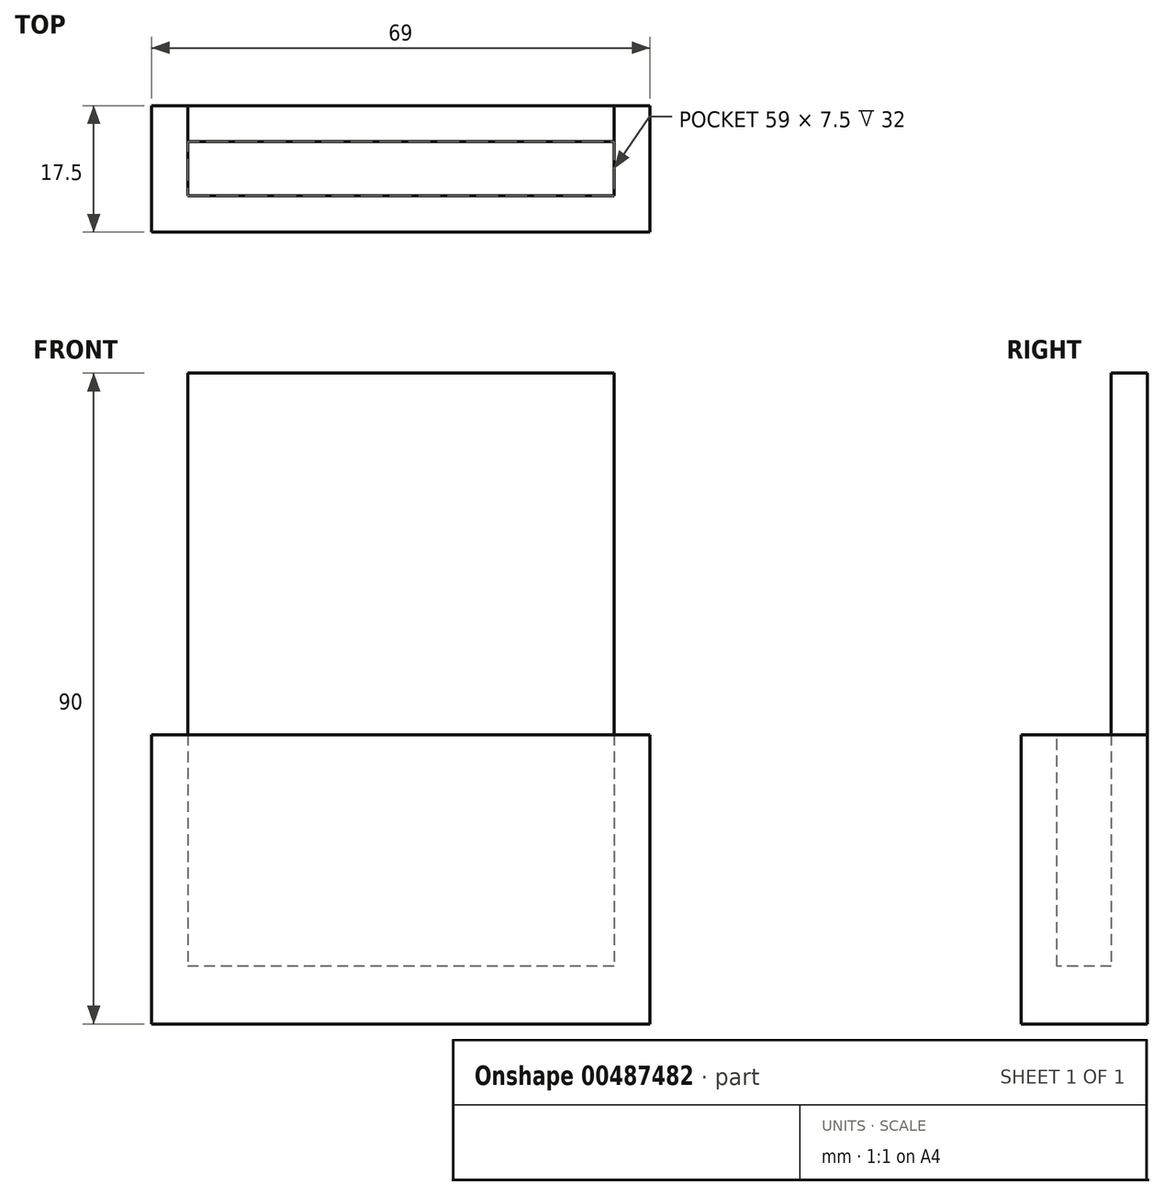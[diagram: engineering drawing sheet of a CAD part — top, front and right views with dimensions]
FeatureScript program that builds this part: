
annotation { "Feature Type Name" : "Feature", "Feature Type Description" : "" }
export const myFeature = defineFeature(function(context is Context, id is Id, definition is map)
    precondition{}
    {
        {
            var Q0;
            Q0=qCreatedBy(makeId("Right.planeOp"),FACE);
            var sketch = newSketch(context, id + "F0", { "sketchPlane" : qUnion([Q0])});
            skLineSegment(sketch, "E0", {"start": v(0, 0) * mm, "end": v(0, 90) * mm});
            skLineSegment(sketch, "E1", {"start": v(0, 90) * mm, "end": v(-5, 90) * mm});
            skLineSegment(sketch, "E2", {"start": v(-5, 90) * mm, "end": v(-5, 8) * mm});
            skLineSegment(sketch, "E3", {"start": v(-5, 8) * mm, "end": v(-12.5, 8) * mm});
            skLineSegment(sketch, "E4", {"start": v(-12.5, 8) * mm, "end": v(-12.5, 40) * mm});
            skLineSegment(sketch, "E5", {"start": v(-12.5, 40) * mm, "end": v(-17.5, 40) * mm});
            skLineSegment(sketch, "E6", {"start": v(-17.5, 40) * mm, "end": v(-17.5, 0) * mm});
            skLineSegment(sketch, "E7", {"start": v(-17.5, 0) * mm, "end": v(0, 0) * mm});
            skSolve(sketch);
        }
        {
            var Q0;
            Q0 = qSketchRegion(id + "F0", true);
            extrude(context, id + "F1", {"entities" : qUnion([Q0]), "depth" : 59 * mm});
        }
        {
            var Q0;
            Q0=makeQuery(id+"F1.opExtrude","CAP_FACE",FACE,{"disambiguationData":[OSD([sQuery(id+"F0.wireOp",EDGE,"E0"),sQuery(id+"F0.wireOp",EDGE,"E1"),sQuery(id+"F0.wireOp",EDGE,"E2"),sQuery(id+"F0.wireOp",EDGE,"E3"),sQuery(id+"F0.wireOp",EDGE,"E4"),sQuery(id+"F0.wireOp",EDGE,"E5"),sQuery(id+"F0.wireOp",EDGE,"E6"),sQuery(id+"F0.wireOp",EDGE,"E7")])],"isStart":false});
            var sketch = newSketch(context, id + "F2", { "sketchPlane" : qUnion([Q0])});
            skLineSegment(sketch, "E8.bottom", {"start": v(-17.5, 40) * mm, "end": v(0, 40) * mm});
            skLineSegment(sketch, "E8.top", {"start": v(-17.5, 0) * mm, "end": v(0, 0) * mm});
            skLineSegment(sketch, "E8.left", {"start": v(-17.5, 40) * mm, "end": v(-17.5, 0) * mm});
            skLineSegment(sketch, "E8.right", {"start": v(0, 40) * mm, "end": v(0, 0) * mm});
            skSolve(sketch);
        }
        {
            var Q0;
            Q0 = qSketchRegion(id + "F2", true);
            extrude(context, id + "F3", {"entities" : qUnion([Q0]), "operationType" : NewBodyOperationType.ADD, "depth" : 5 * mm});
        }
        {
            var Q0;
            Q0=makeQuery(id+"F1.opExtrude","CAP_FACE",FACE,{"disambiguationData":[OSD([sQuery(id+"F0.wireOp",EDGE,"E0"),sQuery(id+"F0.wireOp",EDGE,"E1"),sQuery(id+"F0.wireOp",EDGE,"E2"),sQuery(id+"F0.wireOp",EDGE,"E3"),sQuery(id+"F0.wireOp",EDGE,"E4"),sQuery(id+"F0.wireOp",EDGE,"E5"),sQuery(id+"F0.wireOp",EDGE,"E6"),sQuery(id+"F0.wireOp",EDGE,"E7")])],"isStart":true});
            var sketch = newSketch(context, id + "F4", { "sketchPlane" : qUnion([Q0])});
            skLineSegment(sketch, "E9.bottom", {"start": v(17.5, 0) * mm, "end": v(0, 0) * mm});
            skLineSegment(sketch, "E9.top", {"start": v(17.5, 40) * mm, "end": v(0, 40) * mm});
            skLineSegment(sketch, "E9.left", {"start": v(17.5, 0) * mm, "end": v(17.5, 40) * mm});
            skLineSegment(sketch, "E9.right", {"start": v(0, 0) * mm, "end": v(0, 40) * mm});
            skSolve(sketch);
        }
        {
            var Q0;
            Q0 = qSketchRegion(id + "F4", true);
            extrude(context, id + "F5", {"entities" : qUnion([Q0]), "operationType" : NewBodyOperationType.ADD, "depth" : 5 * mm});
        }
    });
